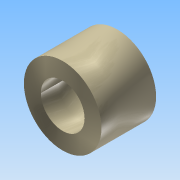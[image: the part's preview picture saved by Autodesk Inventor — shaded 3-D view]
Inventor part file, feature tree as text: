
AUTODESK INVENTOR PART (.ipt)
format: ipt  version: 2015 (Build 190159000, 159)  size: 92,160 bytes
history: native  units: mm
features: extrude x1, sketch x1
ambient origin geometry x8: Origin, YZ Plane, XZ Plane, XY Plane, X Axis, Y Axis, Z Axis, Center Point
bodies: Solide1 (feature_tree)
feature tree (2):
  extrude  "Extrusion1"  Depth=7.1mm
  sketch  "Esquisse1"
